# Revit family: Sink-Under_Counter-Kohler-Langlade-6626_6U
name_source: partatom
category: Plumbing Fixtures
revit_build: Autodesk Revit MEP 2012 (Build: 20110916_2132(x64)
units: mm (PartAtom-declared; Revit-internal decimal feet)

## types (16) — shared parameters
Date Modified = March 13, 2015
Depth = 22 "
Drain Flow = 0 GPM
Drain Radius = 0.75 "
Equipment Abbreviation = LUS
Family Version = 1.0
Height = 9.625 "
Manufacturer = Kohler Company
Model Disclaimer = Contact Kohler Company For More Information
Product Page URL = http://www.us.kohler.com
URL = http://www.us.kohler.com
Width = 33 "
zz Length 4 = 22 "
zz Length 5 = 33 "
zz Length 8 = 9.625 "

## per-type parameters (varying)
| type | Description | Model | Product Material | zz Integer 1 |
| White | Langlade Under-Mount Smart Divide Double-Equal Kitchen Sink With Six Faucet Holes, White | K-6626-6U-0 | Cast Iron - Kohler - White Enamel | 1 |
| Sea Salt | Langlade Under-Mount Smart Divide Double-Equal Kitchen Sink With Six Faucet Holes, Sea Salt | K-6626-6U-FF | Cast Iron - Kohler - Sea Salt Enamel | 5 |
| Biscuit | Langlade Under-Mount Smart Divide Double-Equal Kitchen Sink With Six Faucet Holes, Biscuit | K-6626-6U-96 | Cast Iron - Kohler - Biscuit Enamel | 2 |
| Almond | Langlade Under-Mount Smart Divide Double-Equal Kitchen Sink With Six Faucet Holes, Almond | K-6626-6U-47 | Cast Iron - Kohler - Almond Enamel | 3 |
| Cane Sugar | Langlade Under-Mount Smart Divide Double-Equal Kitchen Sink With Six Faucet Holes, Cane Sugar | K-6626-6U-FD | Cast Iron - Kohler - Cane Sugar Enamel | 6 |
| Ice Grey | Langlade Under-Mount Smart Divide Double-Equal Kitchen Sink With Six Faucet Holes, Ice Grey | K-6626-6U-95 | Cast Iron - Kohler - Ice Grey Enamel | 8 |
| Sandbar | Langlade Under-Mount Smart Divide Double-Equal Kitchen Sink With Six Faucet Holes, Sandbar | K-6626-6U-G9 | Cast Iron - Kohler - Sandbar Enamel | 9 |
| Cashmere | Langlade Under-Mount Smart Divide Double-Equal Kitchen Sink With Six Faucet Holes, Cashmere | K-6626-6U-K4 | Cast Iron - Kohler - Cashmere Enamel | 11 |
| Suede | Langlade Under-Mount Smart Divide Double-Equal Kitchen Sink With Six Faucet Holes, Suede | K-6626-6U-20 | Cast Iron - Kohler - Suede Enamel | 14 |
| Black n Tan | Langlade Under-Mount Smart Divide Double-Equal Kitchen Sink With Six Faucet Holes, Black 'n Tan | K-6626-6U-KA | Cast Iron - Kohler - Black n Tan Enamel | 15 |
| Black | Langlade Under-Mount Smart Divide Double-Equal Kitchen Sink With Six Faucet Holes, Black | K-6626-6U-7 | Cast Iron - Kohler - Black Enamel | 4 |
| Dune | Langlade Under-Mount Smart Divide Double-Equal Kitchen Sink With Six Faucet Holes, Dune | K-6626-6U-NY | Cast Iron - Kohler - Dune Enamel | 7 |
| Mexican Sand | Langlade Under-Mount Smart Divide Double-Equal Kitchen Sink With Six Faucet Holes, Mexican Sand | K-6626-6U-33 | Cast Iron - Kohler - Mexican Sand Enamel | 10 |
| Basalt | Langlade Under-Mount Smart Divide Double-Equal Kitchen Sink With Six Faucet Holes, Basalt | K-6626-6U-FT | Cast Iron - Kohler - Basalt Enamel | 12 |
| Thunder Grey | Langlade Under-Mount Smart Divide Double-Equal Kitchen Sink With Six Faucet Holes, Thunder Grey | K-6626-6U-58 | Cast Iron - Kohler - Thunder Grey Enamel | 13 |
| Caviar | Langlade Under-Mount Smart Divide Double-Equal Kitchen Sink With Six Faucet Holes, Caviar | K-6626-6U-FP | Cast Iron - Kohler - Caviar Enamel | 16 |

## geometry (parser evidence)
native form markers: Blend x24, Sweep x2
no freeform markers — native parametric forms only
